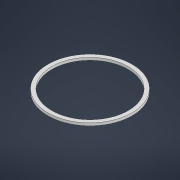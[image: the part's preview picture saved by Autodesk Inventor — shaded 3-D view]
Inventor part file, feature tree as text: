
AUTODESK INVENTOR PART (.ipt)
format: ipt  version: 2022 (Build 260153000, 153)  size: 95,232 bytes
history: native  units: mm
features: extrude x1, sketch x1
ambient origin geometry x8: Origin, YZ Plane, XZ Plane, XY Plane, X Axis, Y Axis, Z Axis, Center Point
bodies: Solid1 (feature_tree)
feature tree (2):
  extrude  "Extrusion1"  Depth=2.0mm TaperAngle=0.0deg
  sketch  "Sketch1"  dims[d0=66.0mm d2=2.0mm d3=0.0mm d4=60.0mm]
